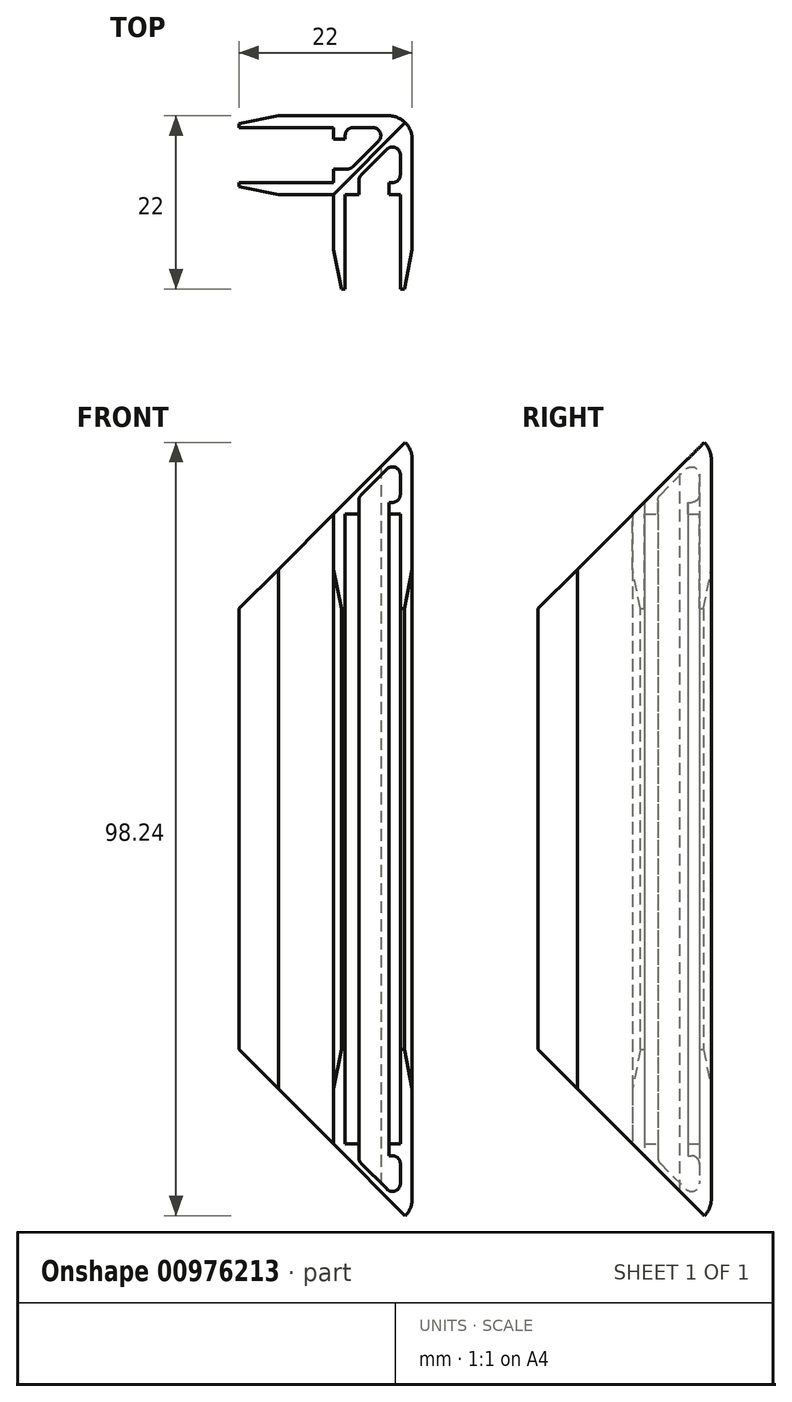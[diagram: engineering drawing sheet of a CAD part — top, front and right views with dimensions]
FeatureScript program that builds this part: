
annotation { "Feature Type Name" : "Feature", "Feature Type Description" : "" }
export const myFeature = defineFeature(function(context is Context, id is Id, definition is map)
    precondition{}
    {
        {
            var Q0;
            Q0=qCreatedBy(makeId("Top.planeOp"),FACE);
            var sketch = newSketch(context, id + "F0", { "sketchPlane" : qUnion([Q0])});
            skLineSegment(sketch, "E0", {"start": v(-22, 0) * mm, "end": v(-3, 0) * mm});
            skLineSegment(sketch, "E1", {"start": v(0, -3) * mm, "end": v(0, -22) * mm});
            skLineSegment(sketch, "E2.0", {"start": v(-10, -10) * mm, "end": v(-10, -22) * mm});
            skLineSegment(sketch, "E2.1", {"start": v(-22, -10) * mm, "end": v(-10, -10) * mm});
            skLineSegment(sketch, "E3.0", {"start": v(-1.5, -2.56) * mm, "end": v(-1.5, -8.5) * mm});
            skLineSegment(sketch, "E3.1", {"start": v(-22, -1.5) * mm, "end": v(-10, -1.5) * mm});
            skLineSegment(sketch, "E4.0", {"start": v(-8.5, -10) * mm, "end": v(-8.5, -22) * mm});
            skLineSegment(sketch, "E4.1", {"start": v(-22, -8.5) * mm, "end": v(-10, -8.5) * mm});
            skLineSegment(sketch, "E5", {"start": v(-22, -8.5) * mm, "end": v(-22, -10) * mm});
            skLineSegment(sketch, "E6", {"start": v(-10, -22) * mm, "end": v(-8.5, -22) * mm});
            skLineSegment(sketch, "E7", {"start": v(-1.5, -22) * mm, "end": v(0, -22) * mm});
            skLineSegment(sketch, "E8", {"start": v(-22, 0) * mm, "end": v(-22, -1.5) * mm});
            skLineSegment(sketch, "E9", {"start": v(-10, -8.5) * mm, "end": v(-10, -6.76) * mm});
            skLineSegment(sketch, "E10", {"start": v(-2.96, -8.5) * mm, "end": v(-1.5, -8.5) * mm});
            skLineSegment(sketch, "E11", {"start": v(-8.5, -10) * mm, "end": v(-6.76, -10) * mm});
            skLineSegment(sketch, "E12.trimOffspring", {"start": v(-8.5, -1.5) * mm, "end": v(-2.56, -1.5) * mm});
            skLineSegment(sketch, "E13.trimOffspring", {"start": v(-1.5, -10) * mm, "end": v(-1.5, -22) * mm});
            skLineSegment(sketch, "E14.0", {"start": v(-6.76, -7.82) * mm, "end": v(-1.5, -2.56) * mm});
            skLineSegment(sketch, "E15.0", {"start": v(-7.82, -6.76) * mm, "end": v(-2.56, -1.5) * mm});
            skLineSegment(sketch, "E16.top", {"start": v(-10, -6.76) * mm, "end": v(-7.82, -6.76) * mm});
            skLineSegment(sketch, "E16.right", {"start": v(-6.76, -10) * mm, "end": v(-6.76, -7.82) * mm});
            skLineSegment(sketch, "E17", {"start": v(-10, -10) * mm, "end": v(0, 0) * mm, "construction": true});
            skLineSegment(sketch, "E18.top", {"start": v(-10, -2.96) * mm, "end": v(-8.5, -2.96) * mm});
            skLineSegment(sketch, "E18.right", {"start": v(-2.96, -10) * mm, "end": v(-2.96, -8.5) * mm});
            skLineSegment(sketch, "E19.trimOffspring", {"start": v(-10, -2.96) * mm, "end": v(-10, -1.5) * mm});
            skLineSegment(sketch, "E20.trimOffspring", {"start": v(-8.5, -2.96) * mm, "end": v(-8.5, -1.5) * mm});
            skLineSegment(sketch, "E21.trimOffspring", {"start": v(-2.96, -10) * mm, "end": v(-1.5, -10) * mm});
            skPoint(sketch, "E22.visualSharp", {"position": v(0, 0) * mm});
            skArc(sketch, "E22.filletArc", {"start": v(0, -3) * mm, "mid": v(-0.88, -0.88) * mm, "end": v(-3, 0) * mm});
            skSolve(sketch);
        }
        {
            var Q0;
            Q0=makeQuery(id+"F0.imprint","IMPRINT",FACE,{"disambiguationData":[TD([[makeQuery(id+"F0.imprint","IMPRINT",EDGE,{"derivedFrom":sQuery(id+"F0.wireOp",EDGE,"E0")}),-1.0]])]});
            extrude(context, id + "F1", {"entities" : qUnion([Q0]), "endBound" : BoundingType.SYMMETRIC, "depth" : 100 * mm, "offsetDistance" : 25 * mm});
        }
        {
            var Q0;
            Q0=makeQuery(id+"F1.opExtrude","SWEPT_EDGE",EDGE,{"disambiguationData":[OSD([sQuery(id+"F0.wireOp",EDGE,"E2.1"),sQuery(id+"F0.wireOp",EDGE,"E5")])]});
            var Q1;
            Q1=makeQuery(id+"F1.opExtrude","SWEPT_EDGE",EDGE,{"disambiguationData":[OSD([sQuery(id+"F0.wireOp",EDGE,"E1"),sQuery(id+"F0.wireOp",EDGE,"E7")])]});
            chamfer(context, id + "F2", {"entities" : qUnion([Q0, Q1]), "chamferType" : ChamferType.TWO_OFFSETS, "width1" : 5 * mm, "oppositeDirection" : false, "width2" : 1 * mm, "tangentPropagation" : true});
        }
        {
            var Q0;
            Q0=makeQuery(id+"F1.opExtrude","SWEPT_EDGE",EDGE,{"disambiguationData":[OSD([sQuery(id+"F0.wireOp",EDGE,"E0"),sQuery(id+"F0.wireOp",EDGE,"E8")])]});
            var Q1;
            Q1=makeQuery(id+"F1.opExtrude","SWEPT_EDGE",EDGE,{"disambiguationData":[OSD([sQuery(id+"F0.wireOp",EDGE,"E2.0"),sQuery(id+"F0.wireOp",EDGE,"E6")])]});
            chamfer(context, id + "F3", {"entities" : qUnion([Q0, Q1]), "chamferType" : ChamferType.TWO_OFFSETS, "width1" : 1 * mm, "oppositeDirection" : false, "width2" : 5 * mm, "tangentPropagation" : true});
        }
        {
            var Q0;
            Q0=makeQuery(id+"F1.opExtrude","SWEPT_EDGE",EDGE,{"disambiguationData":[OSD([sQuery(id+"F0.wireOp",EDGE,"E12.trimOffspring"),sQuery(id+"F0.wireOp",EDGE,"E15.0")])]});
            var Q1;
            Q1=makeQuery(id+"F1.opExtrude","SWEPT_EDGE",EDGE,{"disambiguationData":[OSD([sQuery(id+"F0.wireOp",EDGE,"E3.0"),sQuery(id+"F0.wireOp",EDGE,"E14.0")])]});
            var Q2;
            Q2=makeQuery(id+"F1.opExtrude","SWEPT_EDGE",EDGE,{"disambiguationData":[OSD([sQuery(id+"F0.wireOp",EDGE,"E14.0"),sQuery(id+"F0.wireOp",EDGE,"E16.right")])]});
            var Q3;
            Q3=makeQuery(id+"F1.opExtrude","SWEPT_EDGE",EDGE,{"disambiguationData":[OSD([sQuery(id+"F0.wireOp",EDGE,"E15.0"),sQuery(id+"F0.wireOp",EDGE,"E16.top")])]});
            var Q4;
            Q4=makeQuery(id+"F1.opExtrude","SWEPT_EDGE",EDGE,{"disambiguationData":[OSD([sQuery(id+"F0.wireOp",EDGE,"E3.0"),sQuery(id+"F0.wireOp",EDGE,"E10")])]});
            var Q5;
            Q5=makeQuery(id+"F1.opExtrude","SWEPT_EDGE",EDGE,{"disambiguationData":[OSD([sQuery(id+"F0.wireOp",EDGE,"E12.trimOffspring"),sQuery(id+"F0.wireOp",EDGE,"E20.trimOffspring")])]});
            fillet(context, id + "F4", {"entities" : qUnion([Q0, Q1, Q2, Q3, Q4, Q5]), "radius" : 1 * mm, "tangentPropagation" : true, "allowEdgeOverflow" : false});
        }
        {
            var Q0;
            Q0=qCreatedBy(makeId("Front.planeOp"),FACE);
            var sketch = newSketch(context, id + "F5", { "sketchPlane" : qUnion([Q0])});
            skLineSegment(sketch, "E23", {"start": v(-22, 50) * mm, "end": v(-22, 28) * mm});
            skLineSegment(sketch, "E24", {"start": v(-22, 28) * mm, "end": v(0, 50) * mm});
            skLineSegment(sketch, "E25", {"start": v(0, 50) * mm, "end": v(-22, 50) * mm});
            skLineSegment(sketch, "E26", {"start": v(-22.02, 0) * mm, "end": v(0, 0) * mm, "construction": true});
            skLineSegment(sketch, "E27.MirrorCS", {"start": v(-22, -50) * mm, "end": v(-22, -28) * mm});
            skLineSegment(sketch, "E28.MirrorCS", {"start": v(0, -50) * mm, "end": v(-22, -50) * mm});
            skLineSegment(sketch, "E29.MirrorCS", {"start": v(-22, -28) * mm, "end": v(0, -50) * mm});
            skSolve(sketch);
        }
        {
            var Q0;
            Q0=qCreatedBy(makeId("Right.planeOp"),FACE);
            var sketch = newSketch(context, id + "F6", { "sketchPlane" : qUnion([Q0])});
            skLineSegment(sketch, "E30", {"start": v(0, 50) * mm, "end": v(-22, 50) * mm});
            skLineSegment(sketch, "E31", {"start": v(-22, 50) * mm, "end": v(-22, 28) * mm});
            skLineSegment(sketch, "E32", {"start": v(-22, 28) * mm, "end": v(0, 50) * mm});
            skLineSegment(sketch, "E33", {"start": v(0, 0) * mm, "end": v(-34.5, 0) * mm, "construction": true});
            skLineSegment(sketch, "E34.MirrorCS", {"start": v(0, -50) * mm, "end": v(-22, -50) * mm});
            skLineSegment(sketch, "E35.MirrorCS", {"start": v(-22, -28) * mm, "end": v(0, -50) * mm});
            skLineSegment(sketch, "E36.MirrorCS", {"start": v(-22, -50) * mm, "end": v(-22, -28) * mm});
            skSolve(sketch);
        }
        {
            var Q0;
            Q0 = qSketchRegion(id + "F5", true);
            extrude(context, id + "F7", {"entities" : qUnion([Q0]), "operationType" : NewBodyOperationType.REMOVE, "depth" : 25 * mm, "offsetDistance" : 25 * mm});
        }
        {
            var Q0;
            Q0 = qSketchRegion(id + "F6", true);
            extrude(context, id + "F8", {"entities" : qUnion([Q0]), "operationType" : NewBodyOperationType.REMOVE, "oppositeDirection" : true, "depth" : 25 * mm, "offsetDistance" : 25 * mm});
        }
    });
